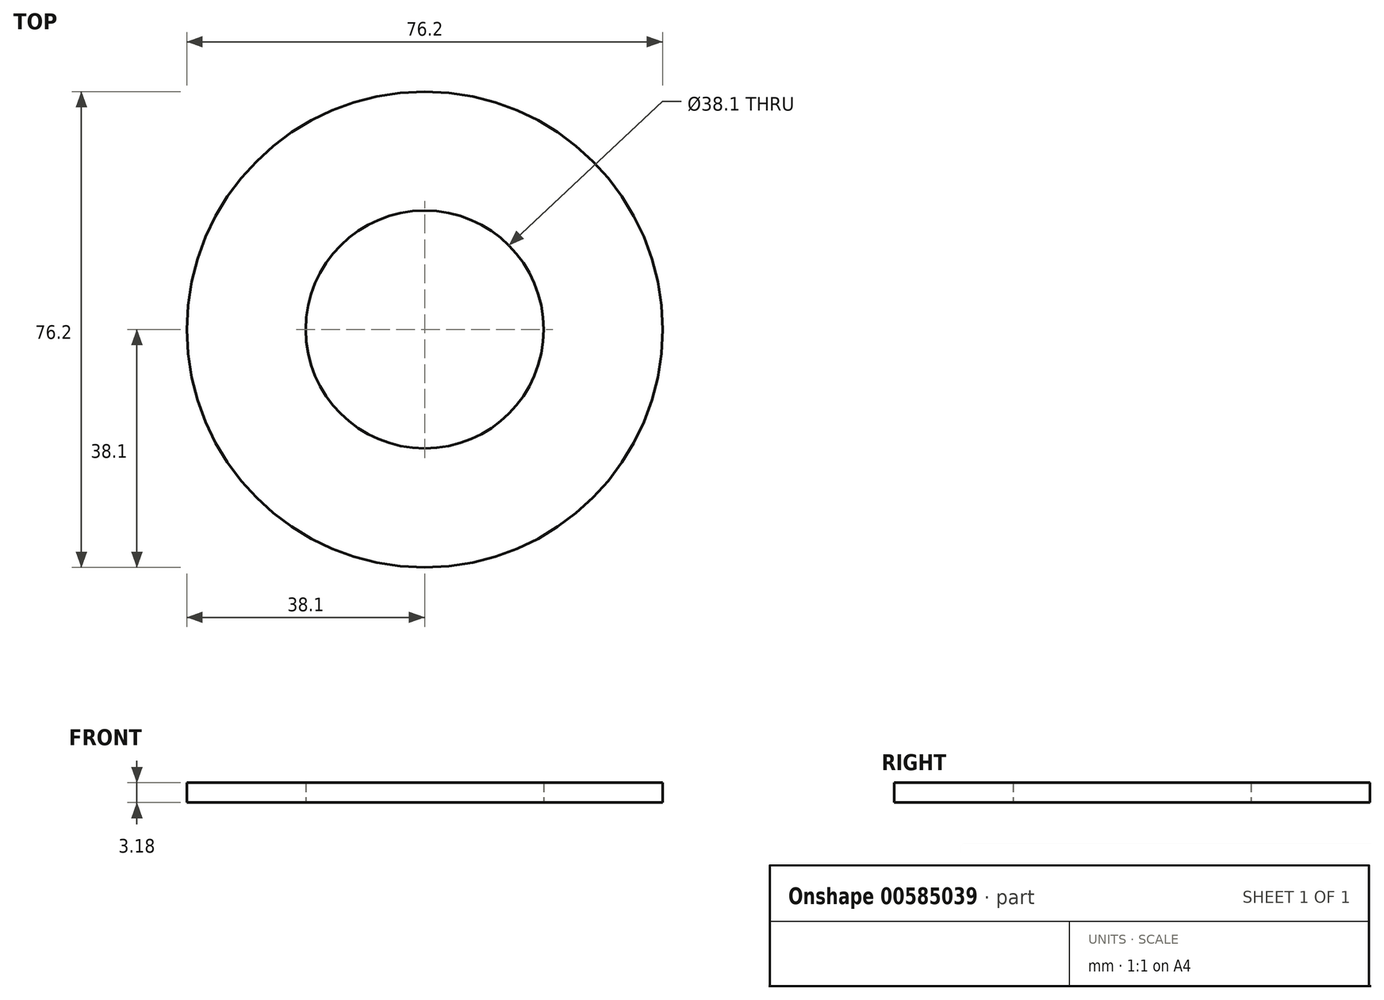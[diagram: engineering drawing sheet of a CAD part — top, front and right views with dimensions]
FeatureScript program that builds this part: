
annotation { "Feature Type Name" : "Feature", "Feature Type Description" : "" }
export const myFeature = defineFeature(function(context is Context, id is Id, definition is map)
    precondition{}
    {
        {
            var Q0;
            Q0=qCreatedBy(makeId("Top.planeOp"),FACE);
            var sketch = newSketch(context, id + "F0", { "sketchPlane" : qUnion([Q0])});
            skCircle(sketch, "E0", {"center": v(0, 0) * mm, "radius": 38.1 * mm});
            skCircle(sketch, "E1", {"center": v(0, 0) * mm, "radius": 19.05 * mm});
            skSolve(sketch);
        }
        {
            var Q0;
            Q0=makeQuery(id+"F0.imprint","IMPRINT",FACE,{"disambiguationData":[TD([[makeQuery(id+"F0.imprint","IMPRINT",EDGE,{"derivedFrom":sQuery(id+"F0.wireOp",EDGE,"E0")}),1.0]])]});
            extrude(context, id + "F1", {"entities" : qUnion([Q0]), "depth" : 3.17 * mm, "offsetDistance" : 25.4 * mm});
        }
    });
